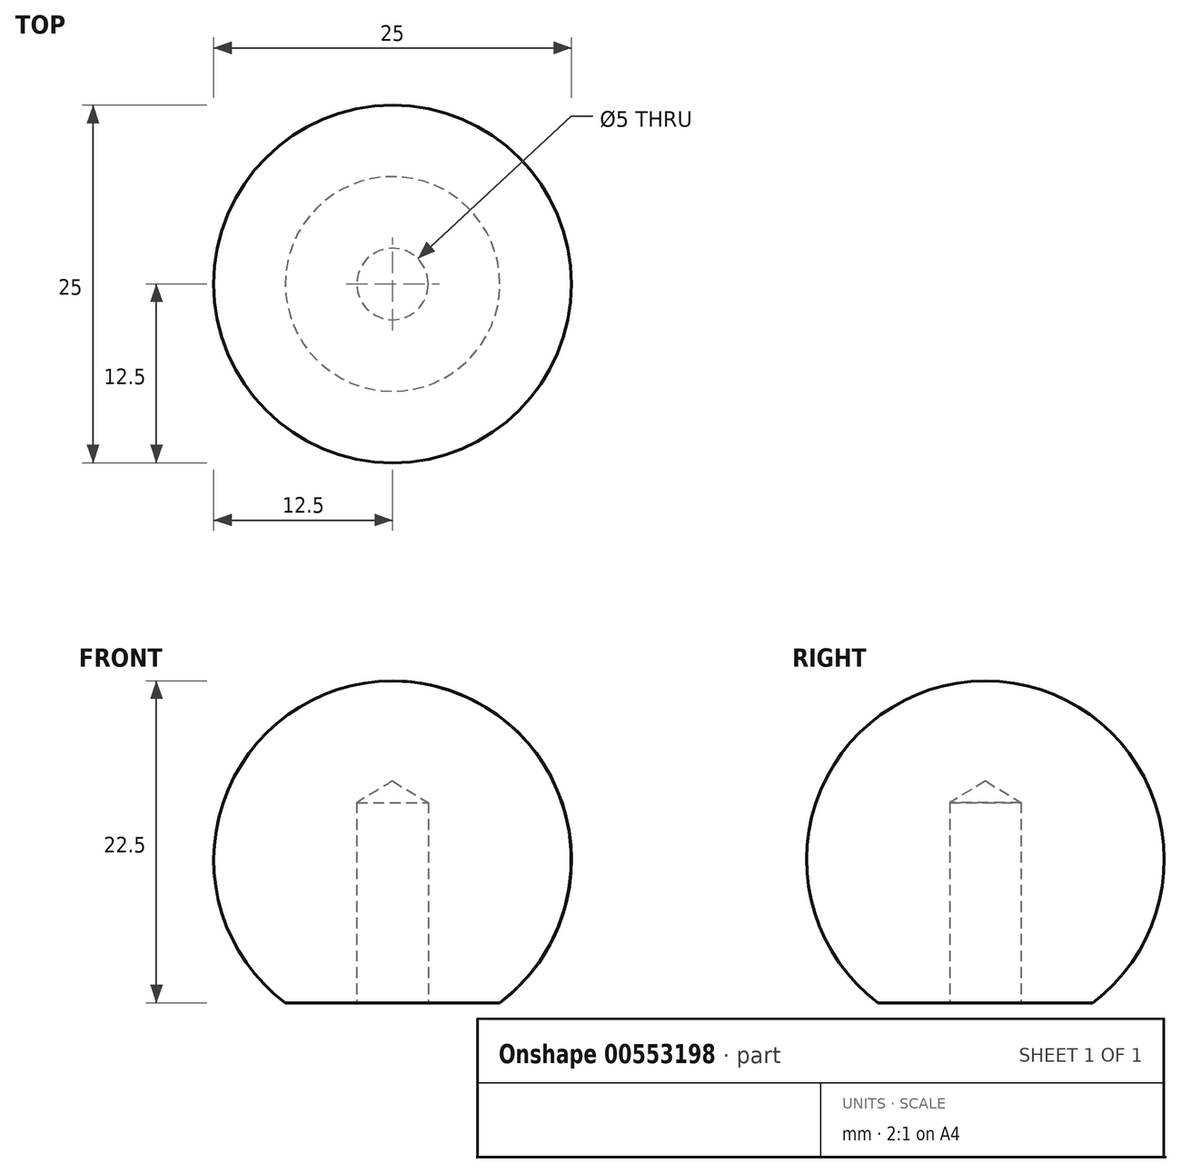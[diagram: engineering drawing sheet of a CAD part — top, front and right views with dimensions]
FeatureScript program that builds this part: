
annotation { "Feature Type Name" : "Feature", "Feature Type Description" : "" }
export const myFeature = defineFeature(function(context is Context, id is Id, definition is map)
    precondition{}
    {
        {
            var Q0;
            Q0=qCreatedBy(makeId("Front.planeOp"),FACE);
            var sketch = newSketch(context, id + "F0", { "sketchPlane" : qUnion([Q0])});
            skArc(sketch, "E0", {"start": v(7.5, -10) * mm, "mid": v(11.86, 3.95) * mm, "end": v(0, 12.5) * mm});
            skLineSegment(sketch, "E1", {"start": v(0, 12.5) * mm, "end": v(0, -10) * mm});
            skLineSegment(sketch, "E2", {"start": v(0, -10) * mm, "end": v(7.5, -10) * mm});
            skSolve(sketch);
        }
        {
            var Q0;
            Q0 = qSketchRegion(id + "F0", true);
            var Q1;
            Q1=sQuery(id+"F0.wireOp",EDGE,"E1");
            revolve(context, id + "F1", {"entities" : qUnion([Q0]), "axis" : qUnion([Q1]), "revolveType" : RevolveType.FULL});
        }
        {
            var Q0;
            Q0=makeQuery(id+"F1.opRevolve","SWEPT_FACE",FACE,{"disambiguationData":[OSD([sQuery(id+"F0.wireOp",EDGE,"E2")])]});
            var sketch = newSketch(context, id + "F2", { "sketchPlane" : qUnion([Q0])});
            skPoint(sketch, "E3", {"position": v(0, 0) * mm});
            skSolve(sketch);
        }
        {
            var Q0;
            Q0=sQuery(id+"F2.wireOp",VERTEX,"E3");
            var Q1;
            Q1=makeQuery(id+"F1.opRevolve","SWEPT_BODY",BODY,{"disambiguationData":[OSD([sQuery(id+"F0.wireOp",EDGE,"E0"),sQuery(id+"F0.wireOp",EDGE,"E1"),sQuery(id+"F0.wireOp",EDGE,"E2")])]});
            hole(context, id + "F3", {"style" : HoleStyle.SIMPLE, "endStyle" : HoleEndStyle.BLIND, "standardTappedOrClearance" : lookupTablePath({ "standard" : "ISO", "engagement" : "75%", "pitch" : "1 mm", "size" : "M6", "type" : "Tapped" }), "standardBlindInLast" : lookupTablePath({ "standard" : "ISO", "engagement" : "75%", "pitch" : "1 mm", "size" : "M6", "type" : "Tapped" }), "holeDiameter" : 5 * mm, "showTappedDepth" : true, "holeDepth" : 14 * mm, "isTappedThrough" : true, "tappedDepth" : 11 * mm, "tapClearance" : 3, "locations" : qUnion([Q0]), "scope" : qUnion([Q1]), "majorDiameter" : 6 * mm});
        }
    });
